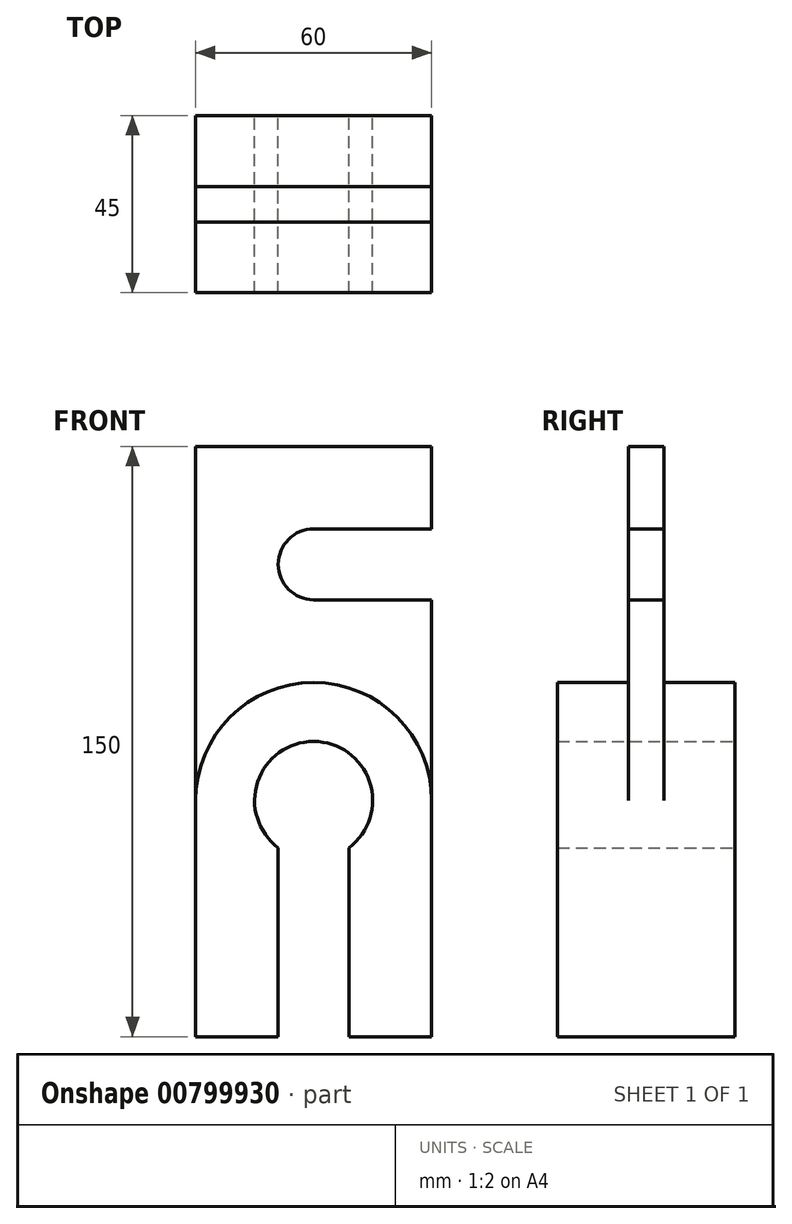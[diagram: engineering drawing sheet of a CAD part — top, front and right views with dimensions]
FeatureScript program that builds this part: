
annotation { "Feature Type Name" : "Feature", "Feature Type Description" : "" }
export const myFeature = defineFeature(function(context is Context, id is Id, definition is map)
    precondition{}
    {
        {
            var Q0;
            Q0=qCreatedBy(makeId("Front.planeOp"),FACE);
            var sketch = newSketch(context, id + "F0", { "sketchPlane" : qUnion([Q0])});
            skCircle(sketch, "E0", {"center": v(0, 0) * mm, "radius": 15 * mm});
            skCircle(sketch, "E1", {"center": v(0, 0) * mm, "radius": 30 * mm});
            skLineSegment(sketch, "E2.top", {"start": v(-30, -60) * mm, "end": v(30, -60) * mm});
            skLineSegment(sketch, "E2.left", {"start": v(-30, 0) * mm, "end": v(-30, -60) * mm});
            skLineSegment(sketch, "E2.right", {"start": v(30, 0) * mm, "end": v(30, -60) * mm});
            skLineSegment(sketch, "E3.top", {"start": v(-9, -60) * mm, "end": v(9, -60) * mm});
            skLineSegment(sketch, "E3.left", {"start": v(-9, -12) * mm, "end": v(-9, -60) * mm});
            skLineSegment(sketch, "E3.right", {"start": v(9, -12) * mm, "end": v(9, -60) * mm});
            skLineSegment(sketch, "E4", {"start": v(0, 0) * mm, "end": v(0, -60) * mm, "construction": true});
            skLineSegment(sketch, "E5.bottom", {"start": v(-30, 0) * mm, "end": v(30, 0) * mm});
            skSolve(sketch);
        }
        {
            var Q0;
            {var subQ0=sQuery(id+"F0.wireOp",EDGE,"E5.bottom");var subQ1=sQuery(id+"F0.wireOp",EDGE,"E0");var subQ2=makeQuery(id+"F0.imprint","INTERSECT",VERTEX,{"disambiguationData":[OD(0.0)],"derivedFrom":[subQ1,subQ0]});Q0=makeQuery(id+"F0.imprint","IMPRINT",FACE,{"disambiguationData":[TD([[makeQuery(id+"F0.imprint","IMPRINT",EDGE,{"disambiguationData":[TD([[subQ2,1.0]])],"derivedFrom":subQ1}),-1.0]])]});}
            var Q1;
            {var subQ0=sQuery(id+"F0.wireOp",EDGE,"E3.right");var subQ1=sQuery(id+"F0.wireOp",EDGE,"E0");var subQ2=makeQuery(id+"F0.imprint","INTERSECT",VERTEX,{"derivedFrom":[subQ1,subQ0]});Q1=makeQuery(id+"F0.imprint","IMPRINT",FACE,{"disambiguationData":[TD([[makeQuery(id+"F0.imprint","IMPRINT",EDGE,{"disambiguationData":[TD([[subQ2,-1.0]])],"derivedFrom":subQ1}),-1.0]])]});}
            var Q2;
            {var subQ0=sQuery(id+"F0.wireOp",EDGE,"E3.left");var subQ1=sQuery(id+"F0.wireOp",EDGE,"E0");var subQ2=makeQuery(id+"F0.imprint","INTERSECT",VERTEX,{"derivedFrom":[subQ1,subQ0]});Q2=makeQuery(id+"F0.imprint","IMPRINT",FACE,{"disambiguationData":[TD([[makeQuery(id+"F0.imprint","IMPRINT",EDGE,{"disambiguationData":[TD([[subQ2,1.0]])],"derivedFrom":subQ1}),-1.0]])]});}
            var Q3;
            {var subQ0=sQuery(id+"F0.wireOp",EDGE,"E2.left");Q3=makeQuery(id+"F0.imprint","IMPRINT",FACE,{"disambiguationData":[TD([[makeQuery(id+"F0.imprint","IMPRINT",EDGE,{"derivedFrom":subQ0}),1.0]])]});}
            var Q4;
            {var subQ0=sQuery(id+"F0.wireOp",EDGE,"E2.right");Q4=makeQuery(id+"F0.imprint","IMPRINT",FACE,{"disambiguationData":[TD([[makeQuery(id+"F0.imprint","IMPRINT",EDGE,{"derivedFrom":subQ0}),-1.0]])]});}
            extrude(context, id + "F1", {"entities" : qUnion([Q0, Q1, Q2, Q3, Q4]), "endBound" : BoundingType.SYMMETRIC, "depth" : 45 * mm, "offsetDistance" : 25.4 * mm});
        }
        {
            var Q0;
            Q0=qCreatedBy(makeId("Front.planeOp"),FACE);
            var sketch = newSketch(context, id + "F2", { "sketchPlane" : qUnion([Q0])});
            skLineSegment(sketch, "E6.top", {"start": v(-30, 0) * mm, "end": v(30, 0) * mm});
            skLineSegment(sketch, "E6.left", {"start": v(-30, 90) * mm, "end": v(-30, 0) * mm});
            skLineSegment(sketch, "E6.right", {"start": v(30, 90) * mm, "end": v(30, 0) * mm});
            skCircle(sketch, "E7", {"center": v(0, 0) * mm, "radius": 30 * mm});
            skCircle(sketch, "E8", {"center": v(0, 135.5) * mm, "radius": 7.5 * mm});
            skCircle(sketch, "E9", {"center": v(0, 135.5) * mm, "radius": 15 * mm});
            skLineSegment(sketch, "E10", {"start": v(0, 150.5) * mm, "end": v(0, 0) * mm, "construction": true});
            skLineSegment(sketch, "E11.top", {"start": v(-30, 90) * mm, "end": v(30, 90) * mm});
            skLineSegment(sketch, "E11.left", {"start": v(-30, 0) * mm, "end": v(-30, 90) * mm});
            skLineSegment(sketch, "E11.right", {"start": v(30, 0) * mm, "end": v(30, 90) * mm});
            skLineSegment(sketch, "E12.bottom", {"start": v(30, 51) * mm, "end": v(0, 51) * mm});
            skLineSegment(sketch, "E12.top", {"start": v(30, 69) * mm, "end": v(0, 69) * mm});
            skLineSegment(sketch, "E12.left", {"start": v(30, 51) * mm, "end": v(30, 69) * mm});
            skLineSegment(sketch, "E12.right", {"start": v(0, 51) * mm, "end": v(0, 69) * mm});
            skCircle(sketch, "E13", {"center": v(0, 60) * mm, "radius": 9 * mm});
            skLineSegment(sketch, "E14", {"start": v(-30, 90) * mm, "end": v(-14.31, 140) * mm});
            skLineSegment(sketch, "E15", {"start": v(30, 90) * mm, "end": v(14.31, 140) * mm});
            skSolve(sketch);
        }
        {
            var Q0;
            {var subQ7=sQuery(id+"F2.wireOp",EDGE,"E11.top");Q0=makeQuery(id+"F2.imprint","IMPRINT",FACE,{"disambiguationData":[TD([[makeQuery(id+"F2.imprint","IMPRINT",EDGE,{"derivedFrom":subQ7}),-1.0]])]});}
            extrude(context, id + "F3", {"entities" : qUnion([Q0]), "operationType" : NewBodyOperationType.ADD, "endBound" : BoundingType.SYMMETRIC, "depth" : 9 * mm, "offsetDistance" : 25.4 * mm});
        }
    });
